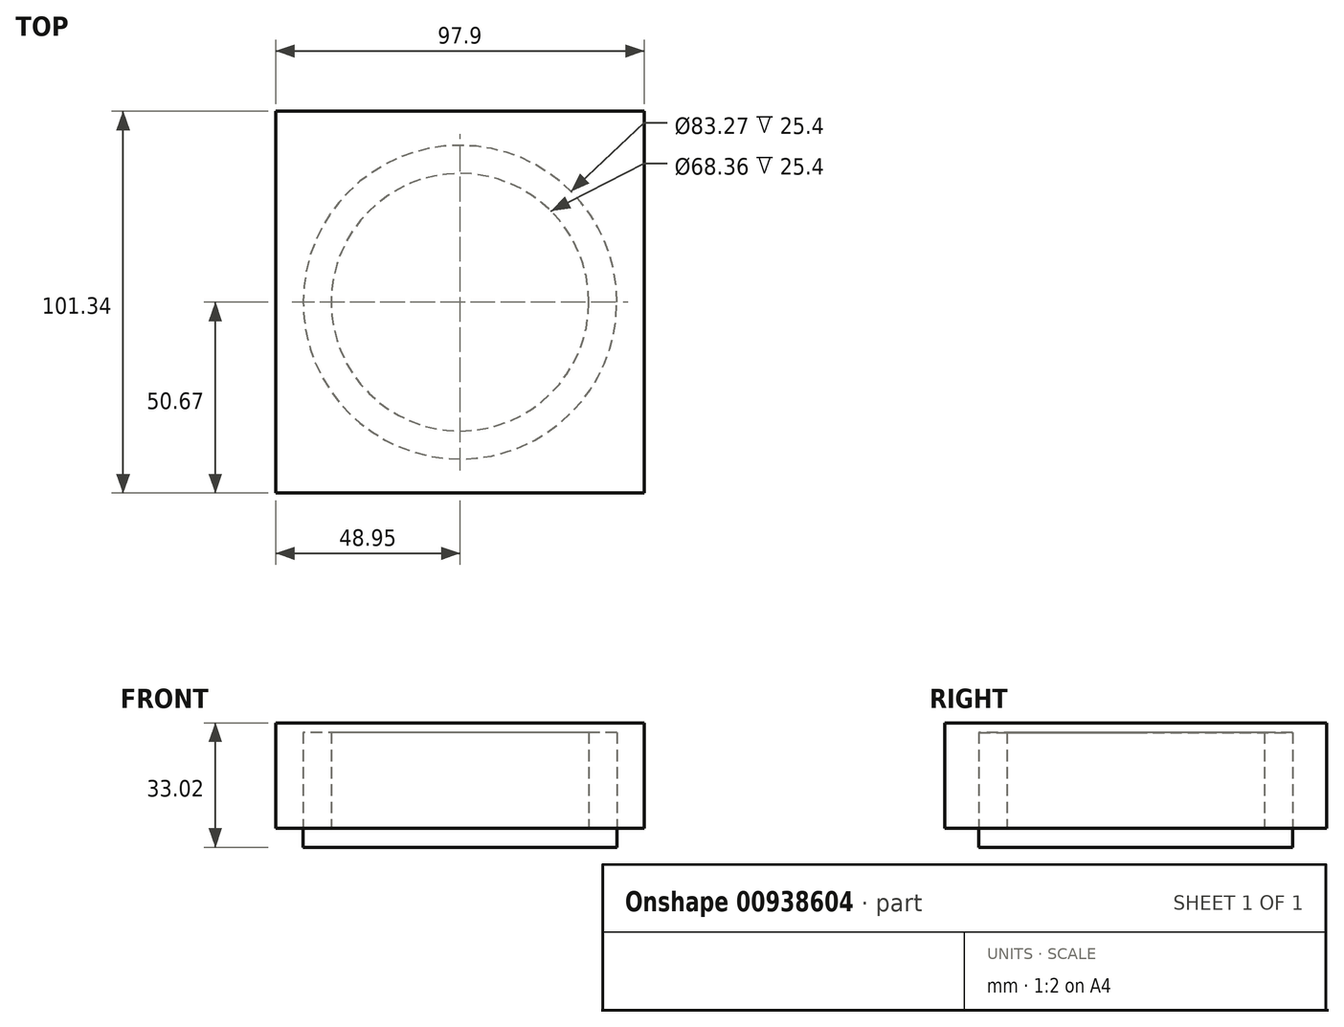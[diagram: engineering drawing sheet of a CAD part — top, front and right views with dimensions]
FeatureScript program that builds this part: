
annotation { "Feature Type Name" : "Feature", "Feature Type Description" : "" }
export const myFeature = defineFeature(function(context is Context, id is Id, definition is map)
    precondition{}
    {
        {
            var Q0;
            Q0=qCreatedBy(makeId("Top.planeOp"),FACE);
            var sketch = newSketch(context, id + "F0", { "sketchPlane" : qUnion([Q0])});
            skCircle(sketch, "E0", {"center": v(0, 0) * mm, "radius": 41.63 * mm});
            skCircle(sketch, "E1", {"center": v(0, 0) * mm, "radius": 34.18 * mm});
            skSolve(sketch);
        }
        {
            var Q0;
            Q0=makeQuery(id+"F0.imprint","IMPRINT",FACE,{"disambiguationData":[TD([[makeQuery(id+"F0.imprint","IMPRINT",EDGE,{"derivedFrom":sQuery(id+"F0.wireOp",EDGE,"E0")}),1.0]])]});
            extrude(context, id + "F1", {"entities" : qUnion([Q0]), "depth" : 25.4 * mm, "offsetDistance" : 25.4 * mm});
        }
        {
            var Q0;
            Q0=makeQuery(id+"F0.imprint","IMPRINT",FACE,{"disambiguationData":[TD([[makeQuery(id+"F0.imprint","IMPRINT",EDGE,{"derivedFrom":sQuery(id+"F0.wireOp",EDGE,"E0")}),1.0]])]});
            var Q1;
            Q1=makeQuery(id+"F0.imprint","IMPRINT",FACE,{"disambiguationData":[TD([[makeQuery(id+"F0.imprint","IMPRINT",EDGE,{"derivedFrom":sQuery(id+"F0.wireOp",EDGE,"E1")}),1.0]])]});
            extrude(context, id + "F2", {"entities" : qUnion([Q0, Q1]), "operationType" : NewBodyOperationType.ADD, "oppositeDirection" : true, "depth" : 5.08 * mm, "offsetDistance" : 25.4 * mm});
        }
        {
            var Q0;
            Q0=makeQuery(id+"F1.opExtrude","CAP_FACE",FACE,{"disambiguationData":[OSD([sQuery(id+"F0.wireOp",EDGE,"E0"),sQuery(id+"F0.wireOp",EDGE,"E1")])],"isStart":false});
            var sketch = newSketch(context, id + "F3", { "sketchPlane" : qUnion([Q0])});
            skLineSegment(sketch, "E2.bottom", {"start": v(-48.95, -50.67) * mm, "end": v(48.95, -50.67) * mm});
            skLineSegment(sketch, "E2.top", {"start": v(-48.95, 50.67) * mm, "end": v(48.95, 50.67) * mm});
            skLineSegment(sketch, "E2.left", {"start": v(-48.95, -50.67) * mm, "end": v(-48.95, 50.67) * mm});
            skLineSegment(sketch, "E2.right", {"start": v(48.95, -50.67) * mm, "end": v(48.95, 50.67) * mm});
            skPoint(sketch, "E2.middle", {"position": v(0, 0) * mm});
            skSolve(sketch);
        }
        {
            var Q0;
            Q0=makeQuery(id+"F3.imprint","IMPRINT",FACE,{"disambiguationData":[TD([[makeQuery(id+"F3.imprint","IMPRINT",EDGE,{"derivedFrom":sQuery(id+"F3.wireOp",EDGE,"E2.bottom")}),1.0]])]});
            var Q1;
            Q1=makeQuery(id+"F3.imprint","IMPRINT",FACE,{"disambiguationData":[TD([[makeQuery(id+"F3.imprint","IMPRINT",EDGE,{"derivedFrom":makeQuery(id+"F1.opExtrude","CAP_EDGE",EDGE,{"disambiguationData":[OSD([sQuery(id+"F0.wireOp",EDGE,"E0")])],"isStart":false})}),1.0]])]});
            var Q2;
            Q2=makeQuery(id+"F3.imprint","IMPRINT",FACE,{"disambiguationData":[TD([[makeQuery(id+"F3.imprint","IMPRINT",EDGE,{"derivedFrom":makeQuery(id+"F1.opExtrude","CAP_EDGE",EDGE,{"disambiguationData":[OSD([sQuery(id+"F0.wireOp",EDGE,"E1")])],"isStart":false})}),1.0]])]});
            extrude(context, id + "F4", {"entities" : qUnion([Q0, Q1, Q2]), "depth" : 2.54 * mm, "offsetDistance" : 25.4 * mm, "hasSecondDirection" : true, "secondDirectionOppositeDirection" : true, "secondDirectionDepth" : 25.4 * mm});
        }
        {
            var Q0;
            Q0=makeQuery(id+"F1.opExtrude","SWEPT_BODY",BODY,{"disambiguationData":[OSD([sQuery(id+"F0.wireOp",EDGE,"E0"),sQuery(id+"F0.wireOp",EDGE,"E1")])]});
            var Q1;
            Q1=makeQuery(id+"F4.opExtrude","SWEPT_BODY",BODY,{"disambiguationData":[OSD([sQuery(id+"F3.wireOp",EDGE,"E2.bottom"),sQuery(id+"F3.wireOp",EDGE,"E2.top"),sQuery(id+"F3.wireOp",EDGE,"E2.left"),sQuery(id+"F3.wireOp",EDGE,"E2.right")])]});
            booleanBodies(context, id + "F5", {"operationType" : BooleanOperationType.SUBTRACTION, "tools" : qUnion([Q0]), "targets" : qUnion([Q1]), "keepTools" : true});
        }
    });
